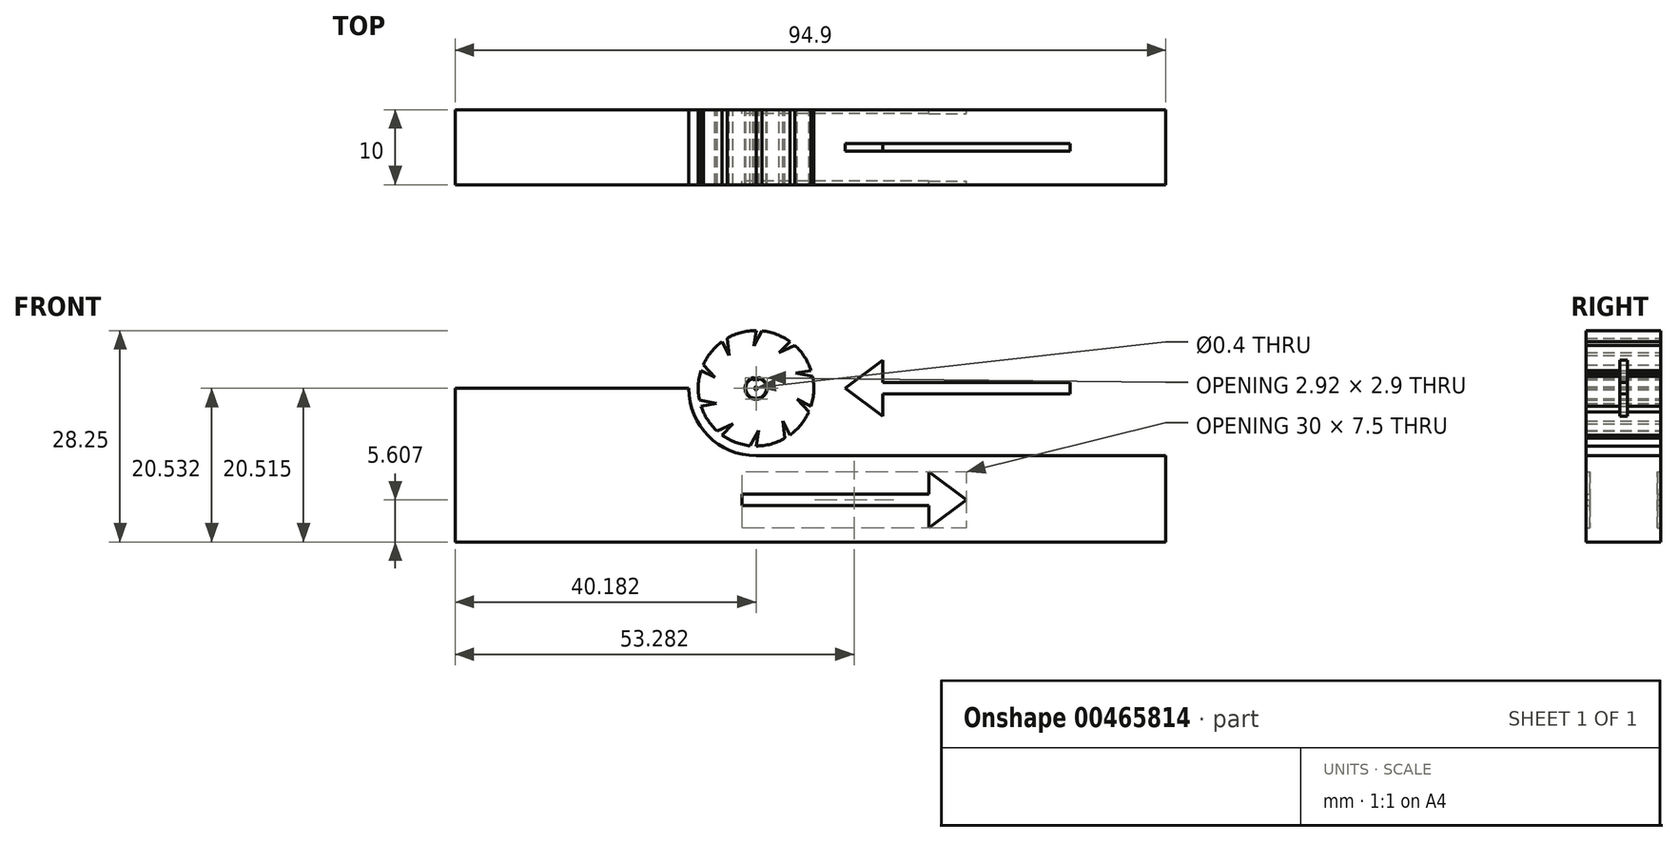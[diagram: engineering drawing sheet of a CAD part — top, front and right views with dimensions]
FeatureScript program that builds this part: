
annotation { "Feature Type Name" : "Feature", "Feature Type Description" : "" }
export const myFeature = defineFeature(function(context is Context, id is Id, definition is map)
    precondition{}
    {
        {
            var Q0;
            Q0=qCreatedBy(makeId("Front.planeOp"),FACE);
            var sketch = newSketch(context, id + "F0", { "sketchPlane" : qUnion([Q0])});
            skLineSegment(sketch, "E0.bottom", {"start": v(14.6, 0) * mm, "end": v(45.78, 0) * mm});
            skLineSegment(sketch, "E0.top", {"start": v(14.6, 20.53) * mm, "end": v(45.78, 20.53) * mm});
            skLineSegment(sketch, "E0.left", {"start": v(14.6, 0) * mm, "end": v(14.6, 20.53) * mm});
            skLineSegment(sketch, "E0.right", {"start": v(45.78, 0) * mm, "end": v(45.78, 20.53) * mm, "construction": true});
            skLineSegment(sketch, "E1.bottom", {"start": v(45.78, 0) * mm, "end": v(109.5, 0) * mm});
            skLineSegment(sketch, "E1.top", {"start": v(45.78, 11.53) * mm, "end": v(109.5, 11.53) * mm});
            skLineSegment(sketch, "E1.left", {"start": v(45.78, 0) * mm, "end": v(45.78, 11.53) * mm, "construction": true});
            skLineSegment(sketch, "E1.right", {"start": v(109.5, 0) * mm, "end": v(109.5, 11.53) * mm});
            skArc(sketch, "E2", {"start": v(45.78, 20.53) * mm, "mid": v(48.42, 14.17) * mm, "end": v(54.78, 11.53) * mm});
            skArc(sketch, "E3", {"start": v(50.25, 26.77) * mm, "mid": v(48.79, 25.39) * mm, "end": v(47.73, 23.67) * mm});
            skLineSegment(sketch, "E4", {"start": v(54.78, 28.25) * mm, "end": v(54.46, 26.18) * mm});
            skLineSegment(sketch, "E5", {"start": v(54.46, 26.18) * mm, "end": v(55.6, 28.2) * mm});
            skLineSegment(sketch, "E6.1.0", {"start": v(50.25, 26.77) * mm, "end": v(51.2, 24.91) * mm});
            skLineSegment(sketch, "E6.1.1", {"start": v(51.2, 24.91) * mm, "end": v(50.93, 27.22) * mm});
            skLineSegment(sketch, "E6.2.0", {"start": v(47.44, 22.92) * mm, "end": v(49.31, 21.97) * mm});
            skLineSegment(sketch, "E6.2.1", {"start": v(49.31, 21.97) * mm, "end": v(47.73, 23.67) * mm});
            skLineSegment(sketch, "E6.3.0", {"start": v(47.44, 18.15) * mm, "end": v(49.5, 18.48) * mm});
            skLineSegment(sketch, "E6.3.1", {"start": v(49.5, 18.48) * mm, "end": v(47.23, 18.93) * mm});
            skLineSegment(sketch, "E6.4.0", {"start": v(50.25, 14.29) * mm, "end": v(51.72, 15.77) * mm});
            skLineSegment(sketch, "E6.4.1", {"start": v(51.72, 15.77) * mm, "end": v(49.62, 14.8) * mm});
            skLineSegment(sketch, "E6.5.0", {"start": v(54.78, 12.82) * mm, "end": v(55.1, 14.88) * mm});
            skLineSegment(sketch, "E6.5.1", {"start": v(55.1, 14.88) * mm, "end": v(53.97, 12.86) * mm});
            skLineSegment(sketch, "E6.6.0", {"start": v(59.32, 14.29) * mm, "end": v(58.36, 16.15) * mm});
            skLineSegment(sketch, "E6.6.1", {"start": v(58.36, 16.15) * mm, "end": v(58.64, 13.85) * mm});
            skLineSegment(sketch, "E6.7.0", {"start": v(62.12, 18.15) * mm, "end": v(60.25, 19.09) * mm});
            skLineSegment(sketch, "E6.7.1", {"start": v(60.25, 19.09) * mm, "end": v(61.83, 17.39) * mm});
            skLineSegment(sketch, "E6.8.0", {"start": v(62.12, 22.92) * mm, "end": v(60.06, 22.58) * mm});
            skLineSegment(sketch, "E6.8.1", {"start": v(60.06, 22.58) * mm, "end": v(62.33, 22.13) * mm});
            skLineSegment(sketch, "E6.9.0", {"start": v(59.32, 26.77) * mm, "end": v(57.85, 25.29) * mm});
            skLineSegment(sketch, "E6.9.1", {"start": v(57.85, 25.29) * mm, "end": v(59.95, 26.26) * mm});
            skArc(sketch, "E7", {"start": v(54.38, 21.85) * mm, "mid": v(54.78, 19.15) * mm, "end": v(55.18, 21.85) * mm});
            skLineSegment(sketch, "E8.bottom", {"start": v(55.18, 21.85) * mm, "end": v(54.38, 21.85) * mm, "construction": true});
            skLineSegment(sketch, "E8.top", {"start": v(55.18, 21.66) * mm, "end": v(54.38, 21.66) * mm});
            skLineSegment(sketch, "E8.left", {"start": v(55.18, 21.85) * mm, "end": v(55.18, 21.66) * mm});
            skLineSegment(sketch, "E8.right", {"start": v(54.38, 21.85) * mm, "end": v(54.38, 21.66) * mm});
            skPoint(sketch, "E8.middle", {"position": v(54.78, 21.75) * mm});
            skLineSegment(sketch, "E9.bottom", {"start": v(71.7, 19.78) * mm, "end": v(96.7, 19.78) * mm});
            skLineSegment(sketch, "E9.top", {"start": v(71.7, 21.28) * mm, "end": v(96.7, 21.28) * mm});
            skLineSegment(sketch, "E9.left", {"start": v(71.7, 19.78) * mm, "end": v(71.7, 21.28) * mm, "construction": true});
            skLineSegment(sketch, "E9.right", {"start": v(96.7, 19.78) * mm, "end": v(96.7, 21.28) * mm});
            skPoint(sketch, "E9.middle", {"position": v(84.2, 20.53) * mm});
            skLineSegment(sketch, "E10", {"start": v(71.7, 19.78) * mm, "end": v(71.7, 16.78) * mm});
            skPoint(sketch, "E11.startSnap0", {"position": v(96.7, 20.53) * mm});
            skLineSegment(sketch, "E12", {"start": v(71.7, 16.78) * mm, "end": v(66.7, 20.53) * mm});
            skLineSegment(sketch, "E13.MirrorCS", {"start": v(71.7, 24.28) * mm, "end": v(66.7, 20.53) * mm});
            skLineSegment(sketch, "E14.MirrorCS", {"start": v(71.7, 21.28) * mm, "end": v(71.7, 24.28) * mm});
            skArc(sketch, "E15.trimOffspring", {"start": v(54.78, 28.25) * mm, "mid": v(52.79, 27.99) * mm, "end": v(50.93, 27.22) * mm});
            skArc(sketch, "E16.trimOffspring", {"start": v(59.32, 26.77) * mm, "mid": v(57.55, 27.73) * mm, "end": v(55.6, 28.2) * mm});
            skArc(sketch, "E17.trimOffspring", {"start": v(62.12, 22.92) * mm, "mid": v(61.26, 24.73) * mm, "end": v(59.95, 26.26) * mm});
            skArc(sketch, "E18.trimOffspring", {"start": v(62.12, 18.15) * mm, "mid": v(62.49, 20.13) * mm, "end": v(62.33, 22.13) * mm});
            skArc(sketch, "E19.trimOffspring", {"start": v(59.32, 14.29) * mm, "mid": v(60.78, 15.67) * mm, "end": v(61.83, 17.39) * mm});
            skArc(sketch, "E20.trimOffspring", {"start": v(54.78, 12.82) * mm, "mid": v(56.78, 13.08) * mm, "end": v(58.64, 13.85) * mm});
            skArc(sketch, "E21.trimOffspring", {"start": v(50.25, 14.29) * mm, "mid": v(52.01, 13.33) * mm, "end": v(53.97, 12.86) * mm});
            skArc(sketch, "E22.trimOffspring", {"start": v(47.44, 18.15) * mm, "mid": v(48.3, 16.33) * mm, "end": v(49.62, 14.8) * mm});
            skArc(sketch, "E23.trimOffspring", {"start": v(47.44, 22.92) * mm, "mid": v(47.08, 20.94) * mm, "end": v(47.23, 18.93) * mm});
            skLineSegment(sketch, "E24.bottom", {"start": v(77.88, 6.36) * mm, "end": v(52.88, 6.36) * mm});
            skLineSegment(sketch, "E24.top", {"start": v(77.88, 4.86) * mm, "end": v(52.88, 4.86) * mm});
            skLineSegment(sketch, "E24.left", {"start": v(77.88, 6.36) * mm, "end": v(77.88, 4.86) * mm, "construction": true});
            skLineSegment(sketch, "E24.right", {"start": v(52.88, 6.36) * mm, "end": v(52.88, 4.86) * mm});
            skPoint(sketch, "E24.middle", {"position": v(65.38, 5.6) * mm});
            skLineSegment(sketch, "E25", {"start": v(77.88, 6.36) * mm, "end": v(77.88, 9.36) * mm});
            skPoint(sketch, "E26.startSnap0", {"position": v(52.88, 5.6) * mm});
            skLineSegment(sketch, "E27", {"start": v(77.88, 9.36) * mm, "end": v(82.88, 5.6) * mm});
            skLineSegment(sketch, "E28.MirrorCS", {"start": v(77.88, 1.86) * mm, "end": v(82.88, 5.6) * mm});
            skLineSegment(sketch, "E29.MirrorCS", {"start": v(77.88, 4.86) * mm, "end": v(77.88, 1.86) * mm});
            skLineSegment(sketch, "E30.0", {"start": v(55.1, 21.75) * mm, "end": v(54.47, 21.75) * mm});
            skLineSegment(sketch, "E30.1", {"start": v(55.1, 21.97) * mm, "end": v(55.1, 21.75) * mm});
            skArc(sketch, "E30.2", {"start": v(54.47, 21.97) * mm, "mid": v(54.78, 19.06) * mm, "end": v(55.1, 21.97) * mm});
            skLineSegment(sketch, "E30.3", {"start": v(54.47, 21.97) * mm, "end": v(54.47, 21.75) * mm});
            skLineSegment(sketch, "E31", {"start": v(54.38, 21.85) * mm, "end": v(55.18, 21.85) * mm});
            skCircle(sketch, "E32", {"center": v(54.78, 20.53) * mm, "radius": 0.2 * mm});
            skSolve(sketch);
        }
        {
            var Q0;
            Q0=makeQuery(id+"F0.imprint","IMPRINT",FACE,{"disambiguationData":[TD([[makeQuery(id+"F0.imprint","IMPRINT",EDGE,{"derivedFrom":sQuery(id+"F0.wireOp",EDGE,"E0.bottom")}),1.0]])]});
            var Q1;
            {var subQ7=sQuery(id+"F0.wireOp",EDGE,"E4");Q1=makeQuery(id+"F0.imprint","IMPRINT",FACE,{"disambiguationData":[TD([[makeQuery(id+"F0.imprint","IMPRINT",EDGE,{"derivedFrom":subQ7}),-1.0]])]});}
            var Q2;
            Q2=makeQuery(id+"F0.imprint","IMPRINT",FACE,{"disambiguationData":[TD([[makeQuery(id+"F0.imprint","IMPRINT",EDGE,{"derivedFrom":sQuery(id+"F0.wireOp",EDGE,"E7")}),1.0]])]});
            extrude(context, id + "F1", {"entities" : qUnion([Q0, Q1, Q2]), "endBound" : BoundingType.SYMMETRIC, "depth" : 10 * mm});
        }
        {
            var Q0;
            Q0=makeQuery(id+"F0.imprint","IMPRINT",FACE,{"disambiguationData":[TD([[makeQuery(id+"F0.imprint","IMPRINT",EDGE,{"derivedFrom":sQuery(id+"F0.wireOp",EDGE,"E24.bottom")}),1.0]])]});
            extrude(context, id + "F2", {"entities" : qUnion([Q0]), "operationType" : NewBodyOperationType.ADD, "endBound" : BoundingType.SYMMETRIC, "oppositeDirection" : true, "depth" : 9 * mm});
        }
        {
            var Q0;
            Q0=makeQuery(id+"F0.imprint","IMPRINT",FACE,{"disambiguationData":[TD([[makeQuery(id+"F0.imprint","IMPRINT",EDGE,{"derivedFrom":sQuery(id+"F0.wireOp",EDGE,"E9.bottom")}),1.0]])]});
            extrude(context, id + "F3", {"entities" : qUnion([Q0]), "endBound" : BoundingType.SYMMETRIC, "depth" : 1 * mm});
        }
        {
            var Q0;
            Q0=makeQuery(id+"F0.imprint","IMPRINT",FACE,{"disambiguationData":[TD([[makeQuery(id+"F0.imprint","IMPRINT",EDGE,{"derivedFrom":sQuery(id+"F0.wireOp",EDGE,"E32")}),1.0]])]});
            extrude(context, id + "F4", {"entities" : qUnion([Q0]), "endBound" : BoundingType.SYMMETRIC, "depth" : 10 * mm});
        }
    });
